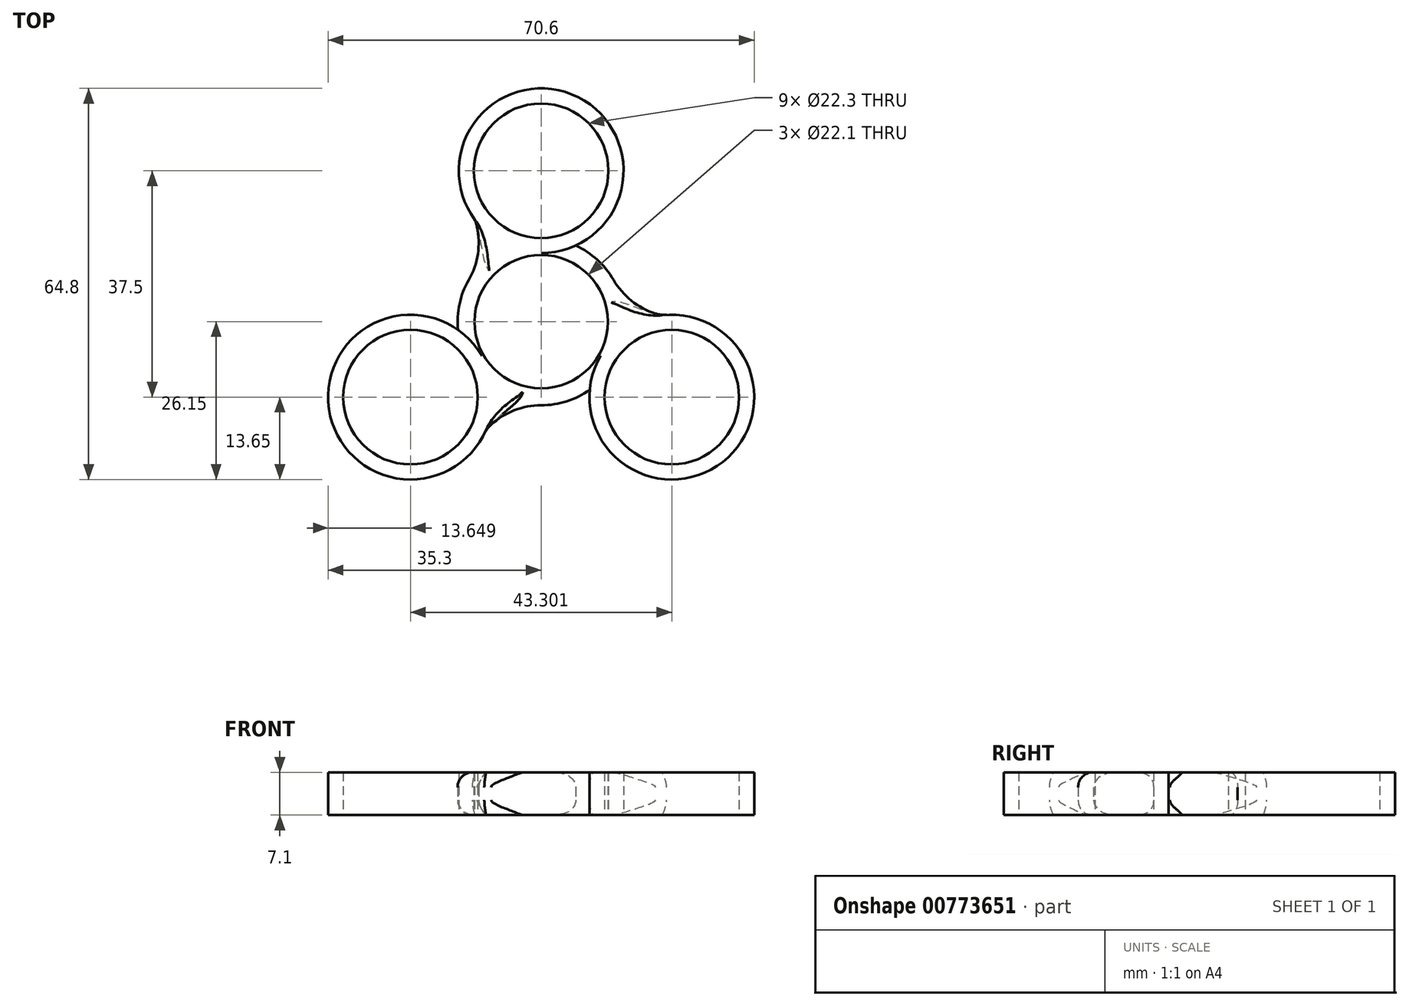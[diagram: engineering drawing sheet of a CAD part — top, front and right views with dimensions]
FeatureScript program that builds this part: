
annotation { "Feature Type Name" : "Feature", "Feature Type Description" : "" }
export const myFeature = defineFeature(function(context is Context, id is Id, definition is map)
    precondition{}
    {
        {
            var Q0;
            Q0=qCreatedBy(makeId("Top.planeOp"),FACE);
            var sketch = newSketch(context, id + "F0", { "sketchPlane" : qUnion([Q0])});
            skCircle(sketch, "E0", {"center": v(0, 0) * mm, "radius": 11.05 * mm});
            skCircle(sketch, "E1.cCircle", {"center": v(0, 0) * mm, "radius": 11.05 * mm, "construction": true});
            skLineSegment(sketch, "E1.0", {"start": v(0, 11.05) * mm, "end": v(9.57, -5.53) * mm});
            skLineSegment(sketch, "E1.1", {"start": v(9.57, -5.52) * mm, "end": v(-9.57, -5.53) * mm});
            skLineSegment(sketch, "E1.2", {"start": v(-9.57, -5.53) * mm, "end": v(0, 11.05) * mm});
            skLineSegment(sketch, "E2", {"start": v(0, 11.05) * mm, "end": v(0, 13.55) * mm});
            skLineSegment(sketch, "E3", {"start": v(9.57, -5.53) * mm, "end": v(12.04, -6.95) * mm});
            skLineSegment(sketch, "E4", {"start": v(-9.57, -5.52) * mm, "end": v(-12, -6.92) * mm});
            skCircle(sketch, "E5.0", {"center": v(0, 0) * mm, "radius": 13.85 * mm});
            skLineSegment(sketch, "E6", {"start": v(0, 13.55) * mm, "end": v(0, 25) * mm});
            skLineSegment(sketch, "E7", {"start": v(-12, -6.92) * mm, "end": v(-21.65, -12.5) * mm});
            skLineSegment(sketch, "E8", {"start": v(12.04, -6.95) * mm, "end": v(21.65, -12.5) * mm});
            skCircle(sketch, "E9", {"center": v(0, 25) * mm, "radius": 11.15 * mm});
            skCircle(sketch, "E10", {"center": v(21.65, -12.5) * mm, "radius": 11.15 * mm});
            skCircle(sketch, "E11", {"center": v(-21.65, -12.5) * mm, "radius": 11.15 * mm});
            skPoint(sketch, "E12", {"position": v(-4.78, 2.76) * mm});
            skCircle(sketch, "E13.0", {"center": v(0, 25) * mm, "radius": 13.65 * mm});
            skCircle(sketch, "E14.0", {"center": v(-21.65, -12.5) * mm, "radius": 13.65 * mm});
            skCircle(sketch, "E15.0", {"center": v(21.65, -12.5) * mm, "radius": 13.65 * mm});
            skLineSegment(sketch, "E16", {"start": v(0, 11.05) * mm, "end": v(0, -51.36) * mm});
            skPoint(sketch, "E16.endSnap0", {"position": v(0, -5.53) * mm});
            skLineSegment(sketch, "E17", {"start": v(-9.57, -5.53) * mm, "end": v(42.9, 24.76) * mm});
            skLineSegment(sketch, "E18", {"start": v(9.57, -5.52) * mm, "end": v(-42.6, 24.6) * mm});
            skPoint(sketch, "E19", {"position": v(4.78, 2.76) * mm});
            skLineSegment(sketch, "E20", {"start": v(11.82, 31.83) * mm, "end": v(33.47, -5.67) * mm});
            skCircle(sketch, "E21", {"center": v(22.65, 13.08) * mm, "radius": 12.3 * mm});
            skLineSegment(sketch, "E22", {"start": v(-11.82, 31.83) * mm, "end": v(-33.47, -5.68) * mm});
            skCircle(sketch, "E23", {"center": v(0, -26.14) * mm, "radius": 12.29 * mm});
            skCircle(sketch, "E24", {"center": v(-22.65, 13.07) * mm, "radius": 12.3 * mm});
            skLineSegment(sketch, "E25", {"start": v(21.65, -26.15) * mm, "end": v(-21.65, -26.15) * mm});
            skSolve(sketch);
        }
        {
            var Q0;
            {var subQ0=sQuery(id+"F0.wireOp",EDGE,"E9");Q0=makeQuery(id+"F0.imprint","IMPRINT",FACE,{"disambiguationData":[TD([[makeQuery(id+"F0.imprint","IMPRINT",EDGE,{"derivedFrom":subQ0}),-1.0]])]});}
            var Q1;
            {var subQ0=sQuery(id+"F0.wireOp",EDGE,"E24");var subQ1=sQuery(id+"F0.wireOp",EDGE,"E13.0");var subQ2=makeQuery(id+"F0.imprint","INTERSECT",VERTEX,{"disambiguationData":[OD(0.0)],"derivedFrom":[subQ1,subQ0]});Q1=makeQuery(id+"F0.imprint","IMPRINT",FACE,{"disambiguationData":[TD([[makeQuery(id+"F0.imprint","IMPRINT",EDGE,{"disambiguationData":[TD([[subQ2,-1.0]])],"derivedFrom":subQ1}),1.0]])]});}
            var Q2;
            {var subQ0=sQuery(id+"F0.wireOp",EDGE,"E21");var subQ1=sQuery(id+"F0.wireOp",EDGE,"E13.0");var subQ2=makeQuery(id+"F0.imprint","INTERSECT",VERTEX,{"disambiguationData":[OD(0.0)],"derivedFrom":[subQ1,subQ0]});Q2=makeQuery(id+"F0.imprint","IMPRINT",FACE,{"disambiguationData":[TD([[makeQuery(id+"F0.imprint","IMPRINT",EDGE,{"disambiguationData":[TD([[subQ2,-1.0]])],"derivedFrom":subQ1}),1.0]])]});}
            var Q3;
            {var subQ0=sQuery(id+"F0.wireOp",EDGE,"E2");Q3=makeQuery(id+"F0.imprint","IMPRINT",FACE,{"disambiguationData":[TD([[makeQuery(id+"F0.imprint","IMPRINT",EDGE,{"derivedFrom":subQ0}),-1.0]])]});}
            var Q4;
            {var subQ0=sQuery(id+"F0.wireOp",EDGE,"E2");Q4=makeQuery(id+"F0.imprint","IMPRINT",FACE,{"disambiguationData":[TD([[makeQuery(id+"F0.imprint","IMPRINT",EDGE,{"derivedFrom":subQ0}),1.0]])]});}
            var Q5;
            {var subQ0=sQuery(id+"F0.wireOp",EDGE,"E13.0");var subQ1=sQuery(id+"F0.wireOp",EDGE,"E5.0");var subQ2=makeQuery(id+"F0.imprint","INTERSECT",VERTEX,{"disambiguationData":[OD(1.0)],"derivedFrom":[subQ1,subQ0]});Q5=makeQuery(id+"F0.imprint","IMPRINT",FACE,{"disambiguationData":[TD([[makeQuery(id+"F0.imprint","IMPRINT",EDGE,{"disambiguationData":[TD([[subQ2,1.0]])],"derivedFrom":subQ0}),-1.0]])]});}
            var Q6;
            {var subQ0=sQuery(id+"F0.wireOp",EDGE,"E13.0");var subQ5=sQuery(id+"F0.wireOp",EDGE,"E5.0");var subQ6=makeQuery(id+"F0.imprint","INTERSECT",VERTEX,{"disambiguationData":[OD(1.0)],"derivedFrom":[subQ5,subQ0]});Q6=makeQuery(id+"F0.imprint","IMPRINT",FACE,{"disambiguationData":[TD([[makeQuery(id+"F0.imprint","IMPRINT",EDGE,{"disambiguationData":[TD([[subQ6,-1.0]])],"derivedFrom":subQ5}),1.0]])]});}
            var Q7;
            {var subQ0=sQuery(id+"F0.wireOp",EDGE,"E13.0");var subQ5=sQuery(id+"F0.wireOp",EDGE,"E5.0");var subQ6=makeQuery(id+"F0.imprint","INTERSECT",VERTEX,{"disambiguationData":[OD(0.0)],"derivedFrom":[subQ5,subQ0]});Q7=makeQuery(id+"F0.imprint","IMPRINT",FACE,{"disambiguationData":[TD([[makeQuery(id+"F0.imprint","IMPRINT",EDGE,{"disambiguationData":[TD([[subQ6,1.0]])],"derivedFrom":subQ5}),1.0]])]});}
            var Q8;
            {var subQ3=sQuery(id+"F0.wireOp",EDGE,"E21");var subQ4=sQuery(id+"F0.wireOp",EDGE,"E5.0");var subQ9=makeQuery(id+"F0.imprint","INTERSECT",VERTEX,{"derivedFrom":[subQ4,subQ3]});Q8=makeQuery(id+"F0.imprint","IMPRINT",FACE,{"disambiguationData":[TD([[makeQuery(id+"F0.imprint","IMPRINT",EDGE,{"disambiguationData":[TD([[subQ9,1.0]])],"derivedFrom":subQ4}),1.0]])]});}
            var Q9;
            {var subQ0=sQuery(id+"F0.wireOp",EDGE,"E21");var subQ1=sQuery(id+"F0.wireOp",EDGE,"E5.0");var subQ2=makeQuery(id+"F0.imprint","INTERSECT",VERTEX,{"derivedFrom":[subQ1,subQ0]});Q9=makeQuery(id+"F0.imprint","IMPRINT",FACE,{"disambiguationData":[TD([[makeQuery(id+"F0.imprint","IMPRINT",EDGE,{"disambiguationData":[TD([[subQ2,1.0]])],"derivedFrom":subQ1}),-1.0]])]});}
            var Q10;
            {var subQ4=sQuery(id+"F0.wireOp",EDGE,"E10");Q10=makeQuery(id+"F0.imprint","IMPRINT",FACE,{"disambiguationData":[TD([[makeQuery(id+"F0.imprint","IMPRINT",EDGE,{"derivedFrom":subQ4}),-1.0]])]});}
            var Q11;
            {var subQ0=sQuery(id+"F0.wireOp",EDGE,"E3");Q11=makeQuery(id+"F0.imprint","IMPRINT",FACE,{"disambiguationData":[TD([[makeQuery(id+"F0.imprint","IMPRINT",EDGE,{"derivedFrom":subQ0}),-1.0]])]});}
            var Q12;
            {var subQ0=sQuery(id+"F0.wireOp",EDGE,"E3");Q12=makeQuery(id+"F0.imprint","IMPRINT",FACE,{"disambiguationData":[TD([[makeQuery(id+"F0.imprint","IMPRINT",EDGE,{"derivedFrom":subQ0}),1.0]])]});}
            var Q13;
            {var subQ0=sQuery(id+"F0.wireOp",EDGE,"E15.0");var subQ5=sQuery(id+"F0.wireOp",EDGE,"E5.0");var subQ6=makeQuery(id+"F0.imprint","INTERSECT",VERTEX,{"disambiguationData":[OD(0.0)],"derivedFrom":[subQ5,subQ0]});Q13=makeQuery(id+"F0.imprint","IMPRINT",FACE,{"disambiguationData":[TD([[makeQuery(id+"F0.imprint","IMPRINT",EDGE,{"disambiguationData":[TD([[subQ6,1.0]])],"derivedFrom":subQ5}),1.0]])]});}
            var Q14;
            {var subQ0=sQuery(id+"F0.wireOp",EDGE,"E14.0");var subQ1=sQuery(id+"F0.wireOp",EDGE,"E4");var subQ2=makeQuery(id+"F0.imprint","INTERSECT",VERTEX,{"derivedFrom":[subQ1,subQ0]});Q14=makeQuery(id+"F0.imprint","IMPRINT",FACE,{"disambiguationData":[TD([[makeQuery(id+"F0.imprint","IMPRINT",EDGE,{"disambiguationData":[TD([[subQ2,1.0]])],"derivedFrom":subQ0}),-1.0]])]});}
            var Q15;
            {var subQ0=sQuery(id+"F0.wireOp",EDGE,"E14.0");var subQ1=sQuery(id+"F0.wireOp",EDGE,"E5.0");var subQ2=makeQuery(id+"F0.imprint","INTERSECT",VERTEX,{"disambiguationData":[OD(1.0)],"derivedFrom":[subQ1,subQ0]});Q15=makeQuery(id+"F0.imprint","IMPRINT",FACE,{"disambiguationData":[TD([[makeQuery(id+"F0.imprint","IMPRINT",EDGE,{"disambiguationData":[TD([[subQ2,1.0]])],"derivedFrom":subQ0}),-1.0]])]});}
            var Q16;
            Q16=makeQuery(id+"F0.imprint","IMPRINT",FACE,{"disambiguationData":[TD([[makeQuery(id+"F0.imprint","IMPRINT",EDGE,{"derivedFrom":sQuery(id+"F0.wireOp",EDGE,"E11")}),-1.0]])]});
            var Q17;
            {var subQ0=sQuery(id+"F0.wireOp",EDGE,"E5.0");var subQ1=sQuery(id+"F0.wireOp",EDGE,"E4");var subQ2=makeQuery(id+"F0.imprint","INTERSECT",VERTEX,{"derivedFrom":[subQ1,subQ0]});Q17=makeQuery(id+"F0.imprint","IMPRINT",FACE,{"disambiguationData":[TD([[makeQuery(id+"F0.imprint","IMPRINT",EDGE,{"disambiguationData":[TD([[subQ2,1.0]])],"derivedFrom":subQ1}),1.0]])]});}
            var Q18;
            {var subQ0=sQuery(id+"F0.wireOp",EDGE,"E5.0");var subQ1=sQuery(id+"F0.wireOp",EDGE,"E4");var subQ2=makeQuery(id+"F0.imprint","INTERSECT",VERTEX,{"derivedFrom":[subQ1,subQ0]});Q18=makeQuery(id+"F0.imprint","IMPRINT",FACE,{"disambiguationData":[TD([[makeQuery(id+"F0.imprint","IMPRINT",EDGE,{"disambiguationData":[TD([[subQ2,1.0]])],"derivedFrom":subQ1}),-1.0]])]});}
            var Q19;
            {var subQ0=sQuery(id+"F0.wireOp",EDGE,"E14.0");var subQ5=sQuery(id+"F0.wireOp",EDGE,"E4");var subQ6=makeQuery(id+"F0.imprint","INTERSECT",VERTEX,{"derivedFrom":[subQ5,subQ0]});Q19=makeQuery(id+"F0.imprint","IMPRINT",FACE,{"disambiguationData":[TD([[makeQuery(id+"F0.imprint","IMPRINT",EDGE,{"disambiguationData":[TD([[subQ6,-1.0]])],"derivedFrom":subQ0}),-1.0]])]});}
            var Q20;
            {var subQ0=sQuery(id+"F0.wireOp",EDGE,"E21");var subQ1=sQuery(id+"F0.wireOp",EDGE,"E15.0");var subQ2=makeQuery(id+"F0.imprint","INTERSECT",VERTEX,{"disambiguationData":[OD(0.0)],"derivedFrom":[subQ1,subQ0]});Q20=makeQuery(id+"F0.imprint","IMPRINT",FACE,{"disambiguationData":[TD([[makeQuery(id+"F0.imprint","IMPRINT",EDGE,{"disambiguationData":[TD([[subQ2,-1.0]])],"derivedFrom":subQ1}),1.0]])]});}
            var Q21;
            {var subQ0=sQuery(id+"F0.wireOp",EDGE,"E23");var subQ1=sQuery(id+"F0.wireOp",EDGE,"E15.0");var subQ2=makeQuery(id+"F0.imprint","INTERSECT",VERTEX,{"disambiguationData":[OD(0.0)],"derivedFrom":[subQ1,subQ0]});Q21=makeQuery(id+"F0.imprint","IMPRINT",FACE,{"disambiguationData":[TD([[makeQuery(id+"F0.imprint","IMPRINT",EDGE,{"disambiguationData":[TD([[subQ2,-1.0]])],"derivedFrom":subQ1}),1.0]])]});}
            var Q22;
            {var subQ0=sQuery(id+"F0.wireOp",EDGE,"E24");var subQ1=sQuery(id+"F0.wireOp",EDGE,"E14.0");var subQ2=makeQuery(id+"F0.imprint","INTERSECT",VERTEX,{"disambiguationData":[OD(0.0)],"derivedFrom":[subQ1,subQ0]});Q22=makeQuery(id+"F0.imprint","IMPRINT",FACE,{"disambiguationData":[TD([[makeQuery(id+"F0.imprint","IMPRINT",EDGE,{"disambiguationData":[TD([[subQ2,-1.0]])],"derivedFrom":subQ1}),1.0]])]});}
            var Q23;
            {var subQ0=sQuery(id+"F0.wireOp",EDGE,"E23");var subQ1=sQuery(id+"F0.wireOp",EDGE,"E14.0");var subQ2=makeQuery(id+"F0.imprint","INTERSECT",VERTEX,{"disambiguationData":[OD(0.0)],"derivedFrom":[subQ1,subQ0]});Q23=makeQuery(id+"F0.imprint","IMPRINT",FACE,{"disambiguationData":[TD([[makeQuery(id+"F0.imprint","IMPRINT",EDGE,{"disambiguationData":[TD([[subQ2,-1.0]])],"derivedFrom":subQ1}),1.0]])]});}
            var Q24;
            {var subQ0=sQuery(id+"F0.wireOp",EDGE,"E15.0");var subQ5=sQuery(id+"F0.wireOp",EDGE,"E5.0");var subQ6=makeQuery(id+"F0.imprint","INTERSECT",VERTEX,{"disambiguationData":[OD(1.0)],"derivedFrom":[subQ5,subQ0]});Q24=makeQuery(id+"F0.imprint","IMPRINT",FACE,{"disambiguationData":[TD([[makeQuery(id+"F0.imprint","IMPRINT",EDGE,{"disambiguationData":[TD([[subQ6,-1.0]])],"derivedFrom":subQ5}),1.0]])]});}
            var Q25;
            {var subQ0=sQuery(id+"F0.wireOp",EDGE,"E15.0");var subQ1=sQuery(id+"F0.wireOp",EDGE,"E5.0");var subQ2=makeQuery(id+"F0.imprint","INTERSECT",VERTEX,{"disambiguationData":[OD(1.0)],"derivedFrom":[subQ1,subQ0]});Q25=makeQuery(id+"F0.imprint","IMPRINT",FACE,{"disambiguationData":[TD([[makeQuery(id+"F0.imprint","IMPRINT",EDGE,{"disambiguationData":[TD([[subQ2,1.0]])],"derivedFrom":subQ0}),-1.0]])]});}
            extrude(context, id + "F1", {"entities" : qUnion([Q0, Q1, Q2, Q3, Q4, Q5, Q6, Q7, Q8, Q9, Q10, Q11, Q12, Q13, Q14, Q15, Q16, Q17, Q18, Q19, Q20, Q21, Q22, Q23, Q24, Q25]), "depth" : 7.1 * mm, "offsetDistance" : 25 * mm});
        }
        {
            var Q0;
            {var subQ0=sQuery(id+"F0.wireOp",EDGE,"E5.0");Q0=makeQuery(id+"F1.opExtrude","CAP_EDGE",EDGE,{"disambiguationData":[OSD([subQ0]),TDD([makeQuery(id+"F0.imprint","IMPRINT",EDGE,{"disambiguationData":[TD([[makeQuery(id+"F0.imprint","INTERSECT",VERTEX,{"disambiguationData":[OD(0.0)],"derivedFrom":[subQ0,sQuery(id+"F0.wireOp",EDGE,"E13.0")]}),1.0]])],"derivedFrom":subQ0})])],"isStart":false});}
            var Q1;
            Q1=makeQuery(id+"F1.opExtrude","CAP_EDGE",EDGE,{"disambiguationData":[OSD([sQuery(id+"F0.wireOp",EDGE,"E21")])],"isStart":false});
            var Q2;
            Q2=makeQuery(id+"F1.opExtrude","CAP_EDGE",EDGE,{"disambiguationData":[OSD([sQuery(id+"F0.wireOp",EDGE,"E24")])],"isStart":false});
            var Q3;
            {var subQ0=sQuery(id+"F0.wireOp",EDGE,"E5.0");Q3=makeQuery(id+"F1.opExtrude","CAP_EDGE",EDGE,{"disambiguationData":[OSD([subQ0]),TDD([makeQuery(id+"F0.imprint","IMPRINT",EDGE,{"disambiguationData":[TD([[makeQuery(id+"F0.imprint","INTERSECT",VERTEX,{"disambiguationData":[OD(0.0)],"derivedFrom":[subQ0,sQuery(id+"F0.wireOp",EDGE,"E14.0")]}),1.0]])],"derivedFrom":subQ0})])],"isStart":false});}
            var Q4;
            Q4=makeQuery(id+"F1.opExtrude","CAP_EDGE",EDGE,{"disambiguationData":[OSD([sQuery(id+"F0.wireOp",EDGE,"E23")])],"isStart":false});
            var Q5;
            {var subQ0=sQuery(id+"F0.wireOp",EDGE,"E5.0");Q5=makeQuery(id+"F1.opExtrude","CAP_EDGE",EDGE,{"disambiguationData":[OSD([subQ0]),TDD([makeQuery(id+"F0.imprint","IMPRINT",EDGE,{"disambiguationData":[TD([[makeQuery(id+"F0.imprint","INTERSECT",VERTEX,{"disambiguationData":[OD(0.0)],"derivedFrom":[subQ0,sQuery(id+"F0.wireOp",EDGE,"E15.0")]}),1.0]])],"derivedFrom":subQ0})])],"isStart":false});}
            var Q6;
            Q6=makeQuery(id+"F1.opExtrude","CAP_EDGE",EDGE,{"disambiguationData":[OSD([sQuery(id+"F0.wireOp",EDGE,"E23")])],"isStart":true});
            var Q7;
            {var subQ0=sQuery(id+"F0.wireOp",EDGE,"E5.0");Q7=makeQuery(id+"F1.opExtrude","CAP_EDGE",EDGE,{"disambiguationData":[OSD([subQ0]),TDD([makeQuery(id+"F0.imprint","IMPRINT",EDGE,{"disambiguationData":[TD([[makeQuery(id+"F0.imprint","INTERSECT",VERTEX,{"disambiguationData":[OD(0.0)],"derivedFrom":[subQ0,sQuery(id+"F0.wireOp",EDGE,"E15.0")]}),1.0]])],"derivedFrom":subQ0})])],"isStart":true});}
            var Q8;
            Q8=makeQuery(id+"F1.opExtrude","CAP_EDGE",EDGE,{"disambiguationData":[OSD([sQuery(id+"F0.wireOp",EDGE,"E24")])],"isStart":true});
            var Q9;
            {var subQ0=sQuery(id+"F0.wireOp",EDGE,"E5.0");Q9=makeQuery(id+"F1.opExtrude","CAP_EDGE",EDGE,{"disambiguationData":[OSD([subQ0]),TDD([makeQuery(id+"F0.imprint","IMPRINT",EDGE,{"disambiguationData":[TD([[makeQuery(id+"F0.imprint","INTERSECT",VERTEX,{"disambiguationData":[OD(0.0)],"derivedFrom":[subQ0,sQuery(id+"F0.wireOp",EDGE,"E14.0")]}),1.0]])],"derivedFrom":subQ0})])],"isStart":true});}
            var Q10;
            {var subQ0=sQuery(id+"F0.wireOp",EDGE,"E5.0");Q10=makeQuery(id+"F1.opExtrude","CAP_EDGE",EDGE,{"disambiguationData":[OSD([subQ0]),TDD([makeQuery(id+"F0.imprint","IMPRINT",EDGE,{"disambiguationData":[TD([[makeQuery(id+"F0.imprint","INTERSECT",VERTEX,{"disambiguationData":[OD(0.0)],"derivedFrom":[subQ0,sQuery(id+"F0.wireOp",EDGE,"E13.0")]}),1.0]])],"derivedFrom":subQ0})])],"isStart":true});}
            var Q11;
            Q11=makeQuery(id+"F1.opExtrude","CAP_EDGE",EDGE,{"disambiguationData":[OSD([sQuery(id+"F0.wireOp",EDGE,"E21")])],"isStart":true});
            fillet(context, id + "F2", {"entities" : qUnion([Q0, Q1, Q2, Q3, Q4, Q5, Q6, Q7, Q8, Q9, Q10, Q11]), "radius" : 2.5 * mm, "tangentPropagation" : true, "allowEdgeOverflow" : false});
        }
        {
            var Q0;
            Q0=makeQuery(id+"F2.opFillet","BLEND_EDGE",EDGE,{"blendedFrom":[makeQuery(id+"F1.opExtrude","CAP_EDGE",EDGE,{"disambiguationData":[OSD([sQuery(id+"F0.wireOp",EDGE,"E24")])],"isStart":false}),makeQuery(id+"F1.opExtrude","SWEPT_FACE",FACE,{"disambiguationData":[OSD([sQuery(id+"F0.wireOp",EDGE,"E13.0")])]})],"blendedInto":[makeQuery(id+"F1.opExtrude","SWEPT_FACE",FACE,{"disambiguationData":[OSD([sQuery(id+"F0.wireOp",EDGE,"E13.0")])]})]});
            var Q1;
            Q1=makeQuery(id+"F2.opFillet","BLEND_EDGE",EDGE,{"blendedFrom":[makeQuery(id+"F1.opExtrude","CAP_EDGE",EDGE,{"disambiguationData":[OSD([sQuery(id+"F0.wireOp",EDGE,"E23")])],"isStart":true}),makeQuery(id+"F1.opExtrude","SWEPT_FACE",FACE,{"disambiguationData":[OSD([sQuery(id+"F0.wireOp",EDGE,"E14.0")])]})],"blendedInto":[makeQuery(id+"F1.opExtrude","SWEPT_FACE",FACE,{"disambiguationData":[OSD([sQuery(id+"F0.wireOp",EDGE,"E14.0")])]})]});
            var Q2;
            Q2=makeQuery(id+"F2.opFillet","BLEND_EDGE",EDGE,{"blendedFrom":[makeQuery(id+"F1.opExtrude","CAP_EDGE",EDGE,{"disambiguationData":[OSD([sQuery(id+"F0.wireOp",EDGE,"E21")])],"isStart":true}),makeQuery(id+"F1.opExtrude","SWEPT_FACE",FACE,{"disambiguationData":[OSD([sQuery(id+"F0.wireOp",EDGE,"E15.0")])]})],"blendedInto":[makeQuery(id+"F1.opExtrude","SWEPT_FACE",FACE,{"disambiguationData":[OSD([sQuery(id+"F0.wireOp",EDGE,"E15.0")])]})]});
            fillet(context, id + "F3", {"entities" : qUnion([Q0, Q1, Q2]), "radius" : 5 * mm, "tangentPropagation" : true, "allowEdgeOverflow" : false});
        }
    });
